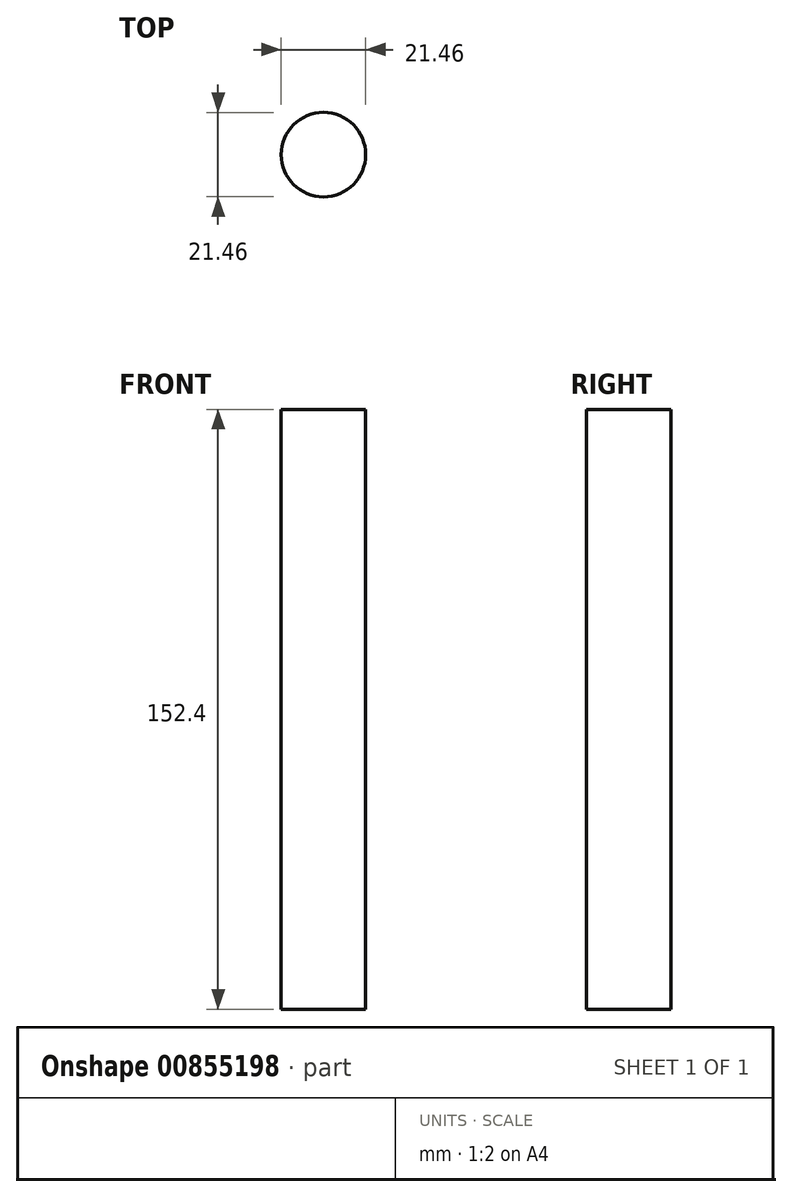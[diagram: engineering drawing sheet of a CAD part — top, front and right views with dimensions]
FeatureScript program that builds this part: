
annotation { "Feature Type Name" : "Feature", "Feature Type Description" : "" }
export const myFeature = defineFeature(function(context is Context, id is Id, definition is map)
    precondition{}
    {
        {
            var Q0;
            Q0=qCreatedBy(makeId("Top.planeOp"),FACE);
            var sketch = newSketch(context, id + "F0", { "sketchPlane" : qUnion([Q0])});
            skCircle(sketch, "E0", {"center": v(0, 0) * mm, "radius": 10.73 * mm});
            skSolve(sketch);
        }
        {
            var Q0;
            Q0=makeQuery(id+"F0.imprint","IMPRINT",FACE,{"disambiguationData":[TD([[makeQuery(id+"F0.imprint","IMPRINT",EDGE,{"derivedFrom":sQuery(id+"F0.wireOp",EDGE,"E0")}),1.0]])]});
            extrude(context, id + "F1", {"entities" : qUnion([Q0]), "depth" : 152.4 * mm, "offsetDistance" : 25.4 * mm});
        }
    });
